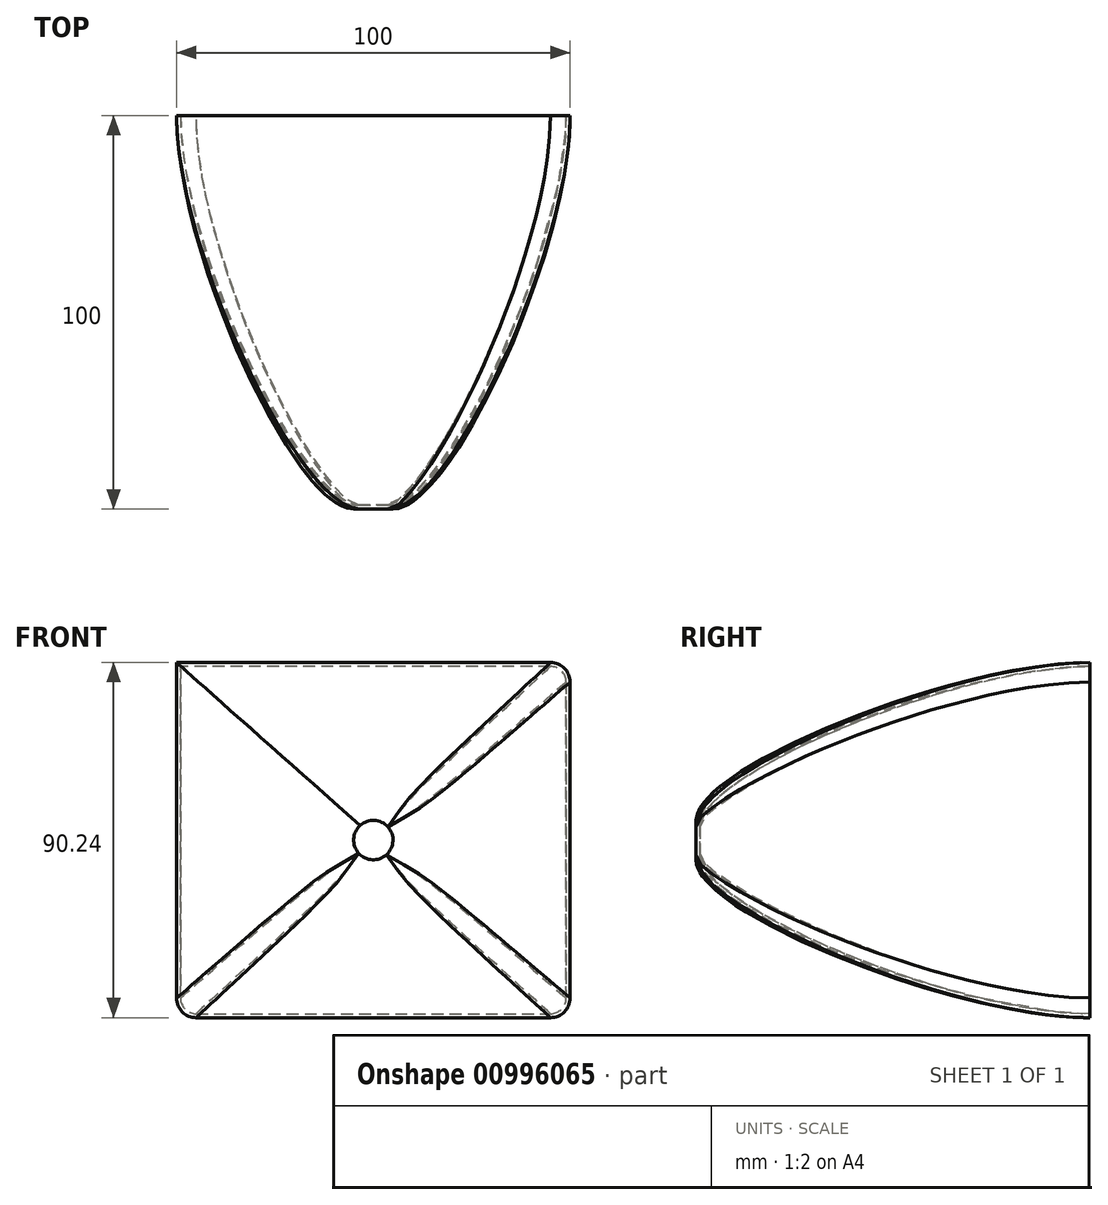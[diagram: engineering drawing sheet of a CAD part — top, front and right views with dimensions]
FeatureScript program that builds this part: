
annotation { "Feature Type Name" : "Feature", "Feature Type Description" : "" }
export const myFeature = defineFeature(function(context is Context, id is Id, definition is map)
    precondition{}
    {
        {
            var Q0;
            Q0=qCreatedBy(makeId("Front.planeOp"),FACE);
            var sketch = newSketch(context, id + "F0", { "sketchPlane" : qUnion([Q0])});
            skLineSegment(sketch, "E0.bottom", {"start": v(50, 45.12) * mm, "end": v(-50, 45.12) * mm});
            skLineSegment(sketch, "E0.top", {"start": v(50, -45.12) * mm, "end": v(-50, -45.12) * mm});
            skLineSegment(sketch, "E0.left", {"start": v(50, 45.12) * mm, "end": v(50, -45.12) * mm});
            skLineSegment(sketch, "E0.right", {"start": v(-50, 45.12) * mm, "end": v(-50, -45.12) * mm});
            skPoint(sketch, "E0.middle", {"position": v(0, 0) * mm});
            skSolve(sketch);
        }
        {
            var Q0;
            Q0=qCreatedBy(makeId("Front.planeOp"),FACE);
            cPlane(context, id + "F1", {"entities" : qUnion([Q0]), "cplaneType" : CPlaneType.OFFSET, "offset" : 100 * mm, "width" : 150 * mm, "height" : 150 * mm});
        }
        {
            var Q0;
            Q0=qCreatedBy(id+"F1.planeOp",FACE);
            var sketch = newSketch(context, id + "F2", { "sketchPlane" : qUnion([Q0])});
            skCircle(sketch, "E1", {"center": v(0, 0) * mm, "radius": 5 * mm});
            skLineSegment(sketch, "E2", {"start": v(15, 15) * mm, "end": v(-15, -15) * mm, "construction": true});
            skLineSegment(sketch, "E3", {"start": v(-15, 15) * mm, "end": v(15, -15) * mm, "construction": true});
            skPoint(sketch, "E4", {"position": v(3.54, 3.54) * mm});
            skPoint(sketch, "E5", {"position": v(-3.54, 3.54) * mm});
            skPoint(sketch, "E6", {"position": v(-3.54, -3.54) * mm});
            skPoint(sketch, "E7", {"position": v(3.54, -3.54) * mm});
            skSolve(sketch);
        }
        {
            var Q0;
            Q0=makeQuery(id+"F0.imprint","IMPRINT",FACE,{"disambiguationData":[TD([[makeQuery(id+"F0.imprint","IMPRINT",EDGE,{"derivedFrom":sQuery(id+"F0.wireOp",EDGE,"E0.bottom")}),1.0]])]});
            var Q1;
            Q1=makeQuery(id+"F2.imprint","IMPRINT",FACE,{"disambiguationData":[TD([[makeQuery(id+"F2.imprint","IMPRINT",EDGE,{"derivedFrom":sQuery(id+"F2.wireOp",EDGE,"E1")}),1.0]])]});
            loft(context, id + "F3", {"startCondition" : LoftEndDerivativeType.NORMAL_TO_PROFILE, "startMagnitude" : 1, "endCondition" : LoftEndDerivativeType.TANGENT_TO_PROFILE, "endMagnitude" : 1, "sheetProfilesArray" : [{ "sheetProfileEntities" : qUnion([Q0]) }, { "sheetProfileEntities" : qUnion([Q1]) }]});
        }
        {
            var Q0;
            Q0=makeQuery(id+"F3.opLoft","SWEPT_EDGE",EDGE,{"disambiguationData":[OSD([sQuery(id+"F0.wireOp",EDGE,"E0.bottom"),sQuery(id+"F0.wireOp",EDGE,"E0.left"),sQuery(id+"F0.wireOp",EDGE,"E0.right"),sQuery(id+"F2.wireOp",EDGE,"E1")])]});
            var Q1;
            Q1=makeQuery(id+"F3.opLoft","SWEPT_EDGE",EDGE,{"disambiguationData":[OSD([sQuery(id+"F0.wireOp",EDGE,"E0.bottom"),sQuery(id+"F0.wireOp",EDGE,"E0.left")])]});
            var Q2;
            Q2=makeQuery(id+"F3.opLoft","SWEPT_EDGE",EDGE,{"disambiguationData":[OSD([sQuery(id+"F0.wireOp",EDGE,"E0.bottom"),sQuery(id+"F0.wireOp",EDGE,"E0.top"),sQuery(id+"F0.wireOp",EDGE,"E0.right"),sQuery(id+"F2.wireOp",EDGE,"E1")])]});
            var Q3;
            Q3=makeQuery(id+"F3.opLoft","SWEPT_EDGE",EDGE,{"disambiguationData":[OSD([sQuery(id+"F0.wireOp",EDGE,"E0.top"),sQuery(id+"F0.wireOp",EDGE,"E0.left"),sQuery(id+"F0.wireOp",EDGE,"E0.right"),sQuery(id+"F2.wireOp",EDGE,"E1")])]});
            fillet(context, id + "F4", {"entities" : qUnion([Q0, Q1, Q2, Q3]), "radius" : 5 * mm, "tangentPropagation" : true, "allowEdgeOverflow" : false});
        }
        {
            var Q0;
            Q0=makeQuery(id+"F3.opLoft","CAP_FACE",FACE,{"disambiguationData":[OSD([makeQuery(id+"F0.imprint","IMPRINT",FACE,{"disambiguationData":[TD([[makeQuery(id+"F0.imprint","IMPRINT",EDGE,{"derivedFrom":sQuery(id+"F0.wireOp",EDGE,"E0.bottom")}),1.0]])]})])],"isStart":true});
            shell(context, id + "F5", {"entities" : qUnion([Q0]), "thickness" : 1 * mm});
        }
    });
